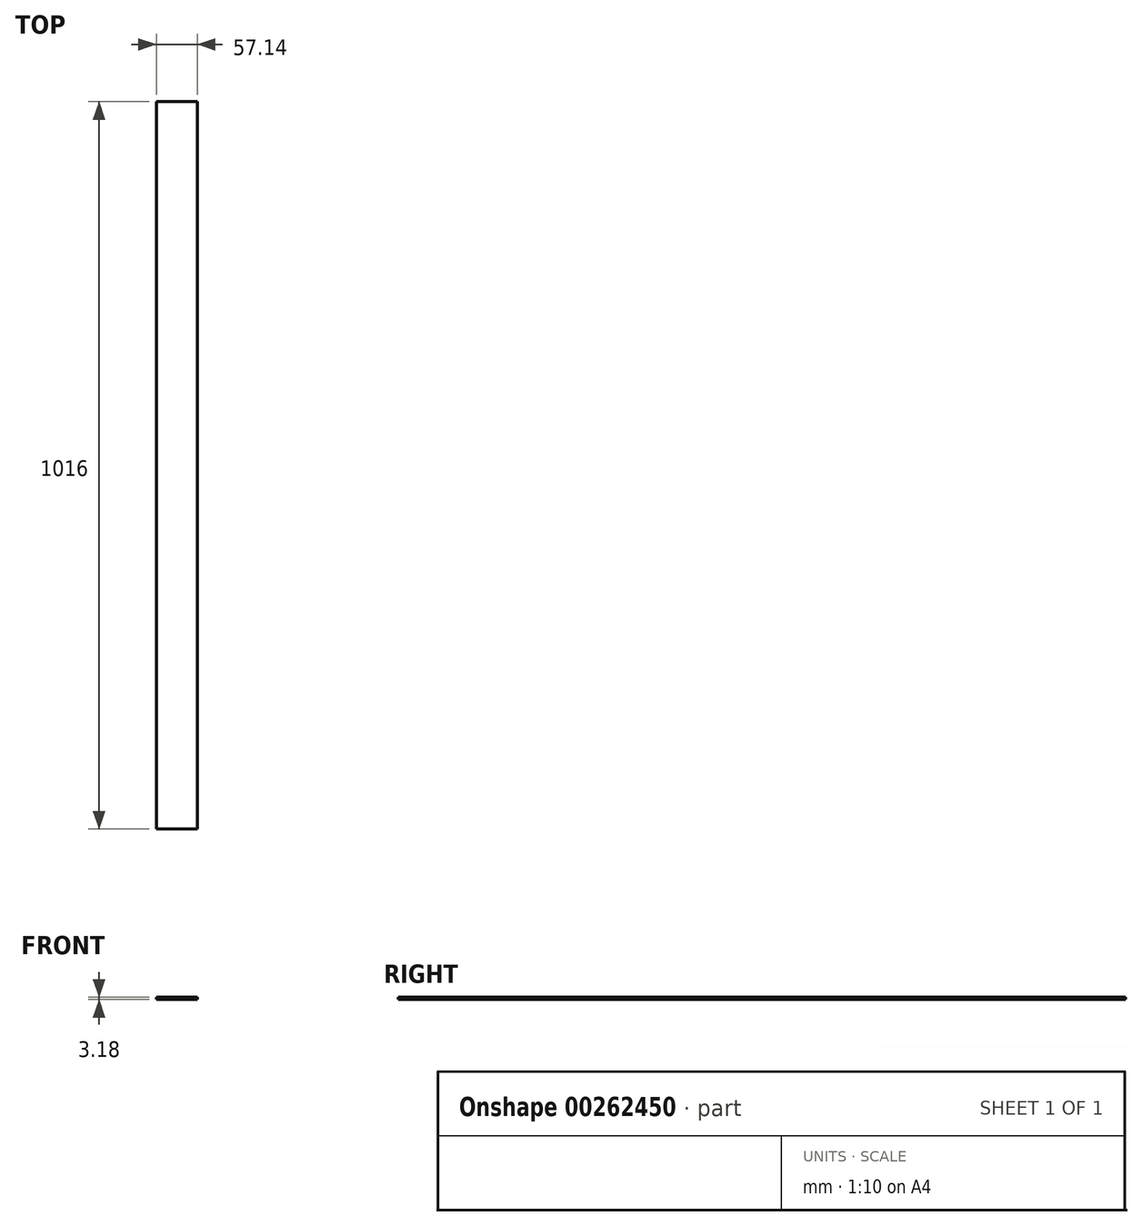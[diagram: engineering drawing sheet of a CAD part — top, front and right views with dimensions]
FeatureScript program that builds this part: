
annotation { "Feature Type Name" : "Feature", "Feature Type Description" : "" }
export const myFeature = defineFeature(function(context is Context, id is Id, definition is map)
    precondition{}
    {
        {
            var Q0;
            Q0=qCreatedBy(makeId("Front.planeOp"),FACE);
            var sketch = newSketch(context, id + "F0", { "sketchPlane" : qUnion([Q0])});
            skLineSegment(sketch, "E0.bottom", {"start": v(28.57, 1.59) * mm, "end": v(-28.58, 1.59) * mm});
            skLineSegment(sketch, "E0.top", {"start": v(28.57, -1.59) * mm, "end": v(-28.58, -1.59) * mm});
            skLineSegment(sketch, "E0.left", {"start": v(28.57, 1.59) * mm, "end": v(28.57, -1.59) * mm});
            skLineSegment(sketch, "E0.right", {"start": v(-28.58, 1.59) * mm, "end": v(-28.58, -1.59) * mm});
            skPoint(sketch, "E0.middle", {"position": v(0, 0) * mm});
            skSolve(sketch);
        }
        {
            var Q0;
            Q0 = qSketchRegion(id + "F0", true);
            extrude(context, id + "F1", {"entities" : qUnion([Q0]), "depth" : 1016 * mm});
        }
    });
